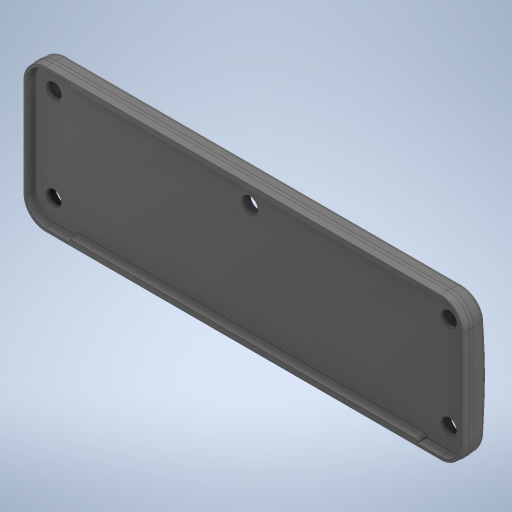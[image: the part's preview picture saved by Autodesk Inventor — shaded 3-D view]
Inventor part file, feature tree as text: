
AUTODESK INVENTOR PART (.ipt)
format: ipt  version: 2023.2 (Build 272271000, 271)  size: 506,368 bytes
history: native  units: mm
features: other x5, sketch x2, reference x2, extrude x1, thicken_offset x1
ambient origin geometry x8: Origin, YZ Plane, XZ Plane, XY Plane, X Axis, Y Axis, Z Axis, Center Point
bodies: Solid2 (feature_tree), Solid1 (feature_tree)
feature tree (11):
  other  "Decal1"
  extrude  "Extrusion1"  Depth=10.0mm
  thicken_offset  "Thicken1"
  sketch  "Sketch1"  dims[d2=10.0mm d3=0.0mm d5=0.2mm]
  other  "Image1"
  sketch  "Sketch2"  dims[d6=0.2mm]
  reference  "Reference1"
  reference  "Reference2"
  parser-record x1  (decoder bookkeeping rows leaked as tree rows — omitted from the tree; the rows remain in map.json)
  other  "ND.NeuroLink._Main.iam"
  other  "1216.1001_head:1"
note: 1 file-system path scrubbed to <path> (originals preserved in map.json)
